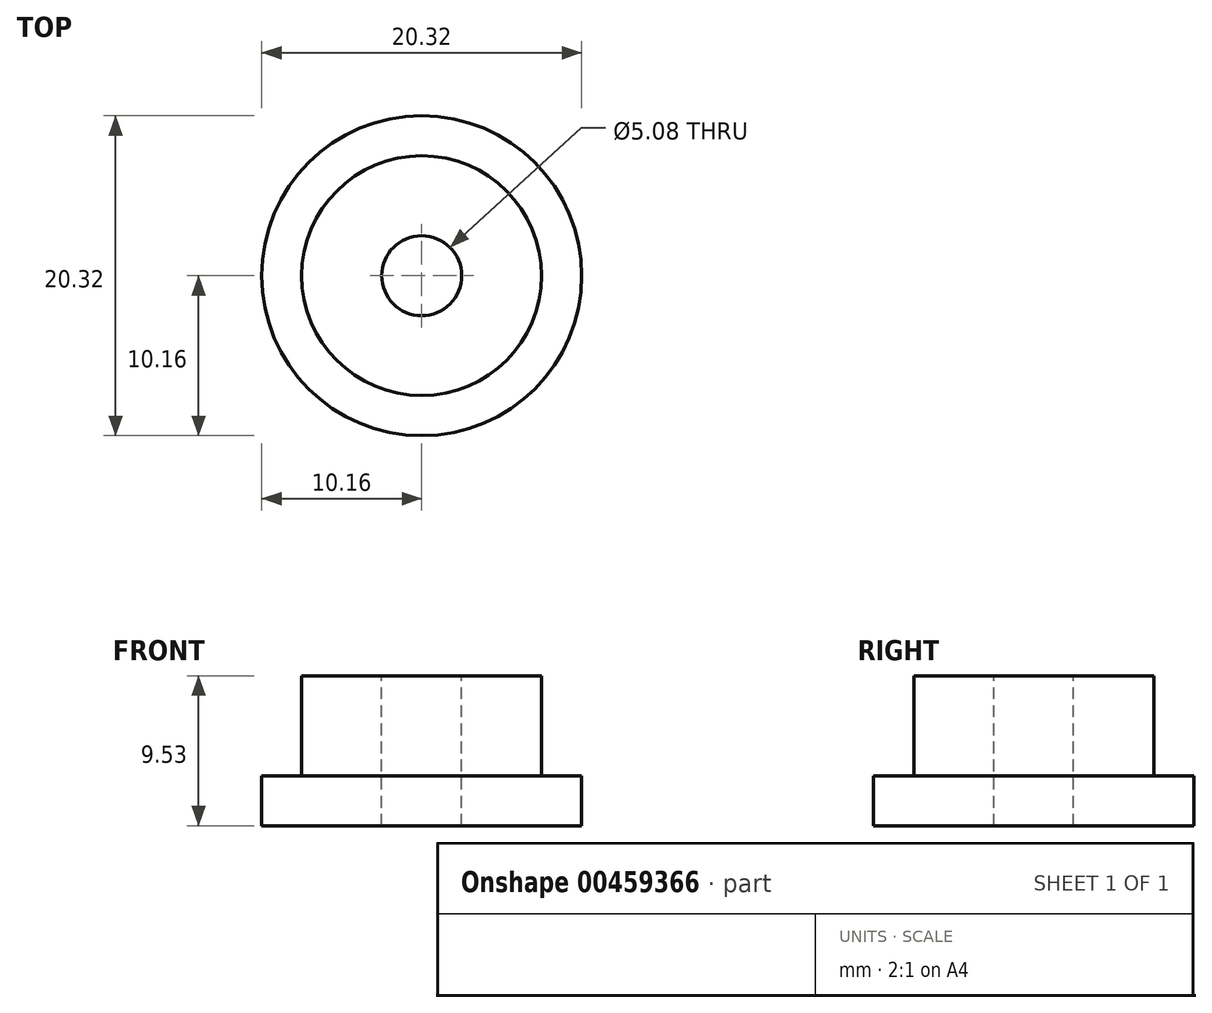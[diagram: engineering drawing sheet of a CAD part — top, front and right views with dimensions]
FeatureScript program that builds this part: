
annotation { "Feature Type Name" : "Feature", "Feature Type Description" : "" }
export const myFeature = defineFeature(function(context is Context, id is Id, definition is map)
    precondition{}
    {
        {
            var Q0;
            Q0=qCreatedBy(makeId("Top.planeOp"),FACE);
            var sketch = newSketch(context, id + "F0", { "sketchPlane" : qUnion([Q0])});
            skCircle(sketch, "E0", {"center": v(0, 0) * mm, "radius": 10.16 * mm});
            skSolve(sketch);
        }
        {
            var Q0;
            Q0=makeQuery(id+"F0.imprint","IMPRINT",FACE,{"disambiguationData":[TD([[makeQuery(id+"F0.imprint","IMPRINT",EDGE,{"derivedFrom":sQuery(id+"F0.wireOp",EDGE,"E0")}),1.0]])]});
            extrude(context, id + "F1", {"entities" : qUnion([Q0]), "depth" : 3.17 * mm});
        }
        {
            var Q0;
            Q0=makeQuery(id+"F1.opExtrude","CAP_FACE",FACE,{"disambiguationData":[OSD([sQuery(id+"F0.wireOp",EDGE,"E0")])],"isStart":false});
            var sketch = newSketch(context, id + "F2", { "sketchPlane" : qUnion([Q0])});
            skCircle(sketch, "E1", {"center": v(0, 0) * mm, "radius": 7.62 * mm});
            skSolve(sketch);
        }
        {
            var Q0;
            Q0=makeQuery(id+"F2.imprint","IMPRINT",FACE,{"disambiguationData":[TD([[makeQuery(id+"F2.imprint","IMPRINT",EDGE,{"derivedFrom":sQuery(id+"F2.wireOp",EDGE,"E1")}),1.0]])]});
            extrude(context, id + "F3", {"entities" : qUnion([Q0]), "operationType" : NewBodyOperationType.ADD, "depth" : 6.35 * mm});
        }
        {
            var Q0;
            Q0=makeQuery(id+"F3.opExtrude","CAP_FACE",FACE,{"disambiguationData":[OSD([sQuery(id+"F2.wireOp",EDGE,"E1")])],"isStart":false});
            var sketch = newSketch(context, id + "F4", { "sketchPlane" : qUnion([Q0])});
            skCircle(sketch, "E2", {"center": v(0, 0) * mm, "radius": 2.54 * mm});
            skSolve(sketch);
        }
        {
            var Q0;
            Q0 = qSketchRegion(id + "F4", true);
            extrude(context, id + "F5", {"entities" : qUnion([Q0]), "operationType" : NewBodyOperationType.REMOVE, "endBound" : BoundingType.UP_TO_NEXT, "oppositeDirection" : true, "depth" : 25 * mm});
        }
    });
